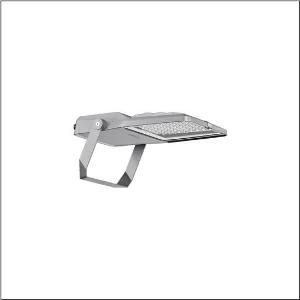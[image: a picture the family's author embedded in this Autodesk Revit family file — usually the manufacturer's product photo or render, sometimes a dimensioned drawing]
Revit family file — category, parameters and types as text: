
# Revit family: floodlight_fl_21_iq_mini___pl43_5xa7772b5a1a_c178
name_source: partatom
category: Lighting Fixtures
units: mm (PartAtom-declared; Revit-internal decimal feet)

## family parameters
Cut with Voids When Loaded = No
Host = Face
Light Source = No
Part Type = Normal
Room Calculation Point = No
Round Connector Dimension = Use Diameter
Shared = No

## types (1)
- --- (1 x LED, 5970 lm, 45.5 W, 4000K)
    Apparent Load = 46 VA
    CIE Flux Codes = 27 78 99 100 100
    Color Rendering = 80
    Color Temperature = 4000K
    Default Elevation = 1800 mm
    Description = Floodlight FL 21 iQ mini, floodlight, primary light control with lens, of PMMA, primary optical cover: protective disc, of toughened safety glass, transparent, light distribution: PL43, light emission: direct distribution, installation type: surface-mounted, LED, High Power LED, rated luminous flux: 5.970lm, luminous efficacy: 131lm/W, light colour: 840, colour temperature: 4000K, control: Street-Remote, Auto-Match, Temp-Guard, Night-Set, Smart-Wire, Desk-Remote (wireless, voltage-free reading and setting of iQ features in the workshop via application-optimized NFC function/RFID function), optimised constant luminous flux control (CLO 2.0), with terminal, 6-pole, mains connection: 220..240V, AC, 50/60Hz, start of lifetime: 46W, end of service life: 48W, reduction: 22W, luminaire housing, of diecast aluminium, powder-coated, Siteco® metallic grey (DB 702S), corrosivity category C5 mid according to DIN EN ISO 12944, sealing non-destructively replaceable, mounting bracket, of steel, galvanised, powder-coated, Siteco® metallic grey (DB 702S), protection rating (complete): IP66, insulation class (complete): insulation class II (safety insulation), certification: CE, ENEC, VDE, protection symbol: D, impact resistance: IK08, permissible operating ambient temperature: -40..+40°C, permissible operating ambient temperature for outdoor applications: -40..+50°C, standard: DIN EN 12944, LABS conformity tested according to VDMA 24364:2018-05, packaging unit: 1 piece

Light Distribution: PL43
    Height = 70 mm
    Lamp = 1 x LED
    Lamp Light Flux = 5970 lm
    Lamp Power = 45.5 W
    Lamp count = 1
    Length = 485 mm
    Luminous efficacy = 131 lm/W
    Manufacturer = Siteco
    ModVariant = No
    Model = 5XA7772B5A1A
    Number of Poles = 1
    OnlyDefault = Yes
    Power Factor = 1
    Product Name = Floodlight FL 21 iQ mini | PL43
    Product group = floodlight | pylon annexe
    ProductGroupID = 6200
    Protection Class = Protection class II
    Protection Degree = IP 66
    RLX_Detail_Level = 1
    RLX_Emergency_Light_Flux = 0 lm
    RLX_Emergency_Type = 0
    RLX_Emergency_Type_DB = No
    RlxData = <blob elided: 96117 chars, md5=5a4c7a7c>
    Socket = socket
    Standby Power = 0 W
    System Light Flux = 5970 lm
    System Power = 46 W
    Type Comments = factory setting: luminous flux: 100 % | dim-lin: 254 | 463 mA
    Type Image = l_1006845.jpg
    URL = http://relux.com
    VarID = @adj_112797
    Voltage = 0 V
    Weight = 0.00 kg
    Width = 337 mm

## geometry (parser evidence)
native form markers: Blend x4, Sweep x13
no freeform markers — native parametric forms only
